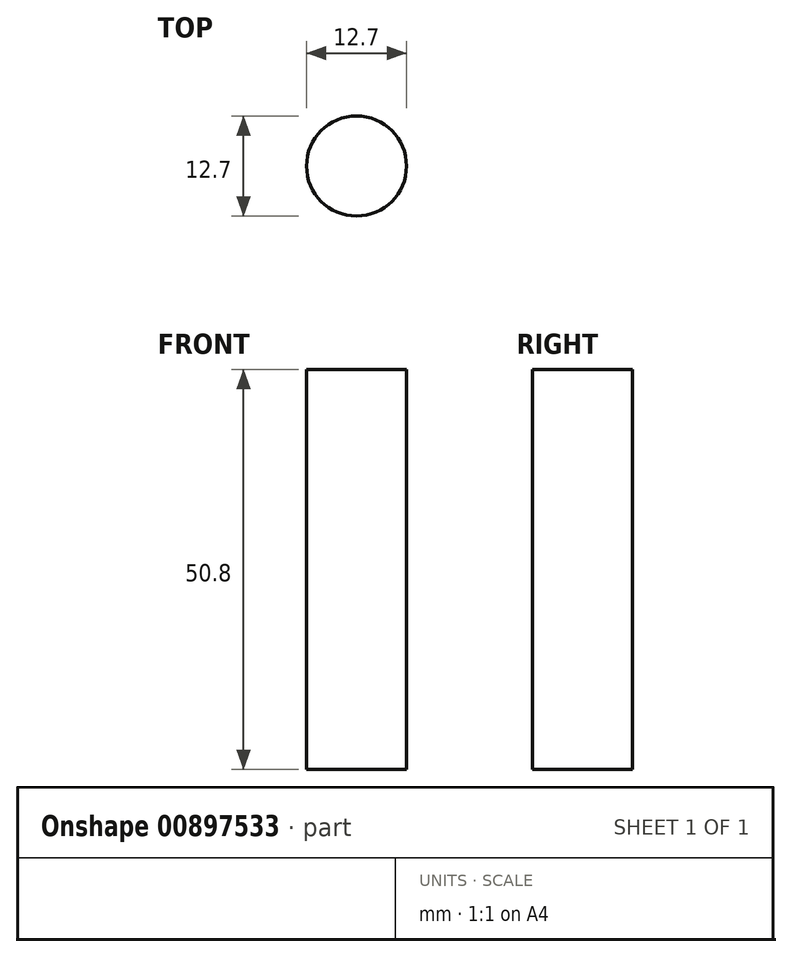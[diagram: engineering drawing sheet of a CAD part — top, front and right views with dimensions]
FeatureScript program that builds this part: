
annotation { "Feature Type Name" : "Feature", "Feature Type Description" : "" }
export const myFeature = defineFeature(function(context is Context, id is Id, definition is map)
    precondition{}
    {
        {
            var Q0;
            Q0=qCreatedBy(makeId("Top.planeOp"),FACE);
            var sketch = newSketch(context, id + "F0", { "sketchPlane" : qUnion([Q0])});
            skCircle(sketch, "E0", {"center": v(0, 0) * mm, "radius": 6.35 * mm});
            skSolve(sketch);
        }
        {
            var Q0;
            Q0=makeQuery(id+"F0.imprint","IMPRINT",FACE,{"disambiguationData":[TD([[makeQuery(id+"F0.imprint","IMPRINT",EDGE,{"derivedFrom":sQuery(id+"F0.wireOp",EDGE,"E0")}),1.0]])]});
            extrude(context, id + "F1", {"entities" : qUnion([Q0]), "depth" : 50.8 * mm, "offsetDistance" : 25.4 * mm});
        }
    });
